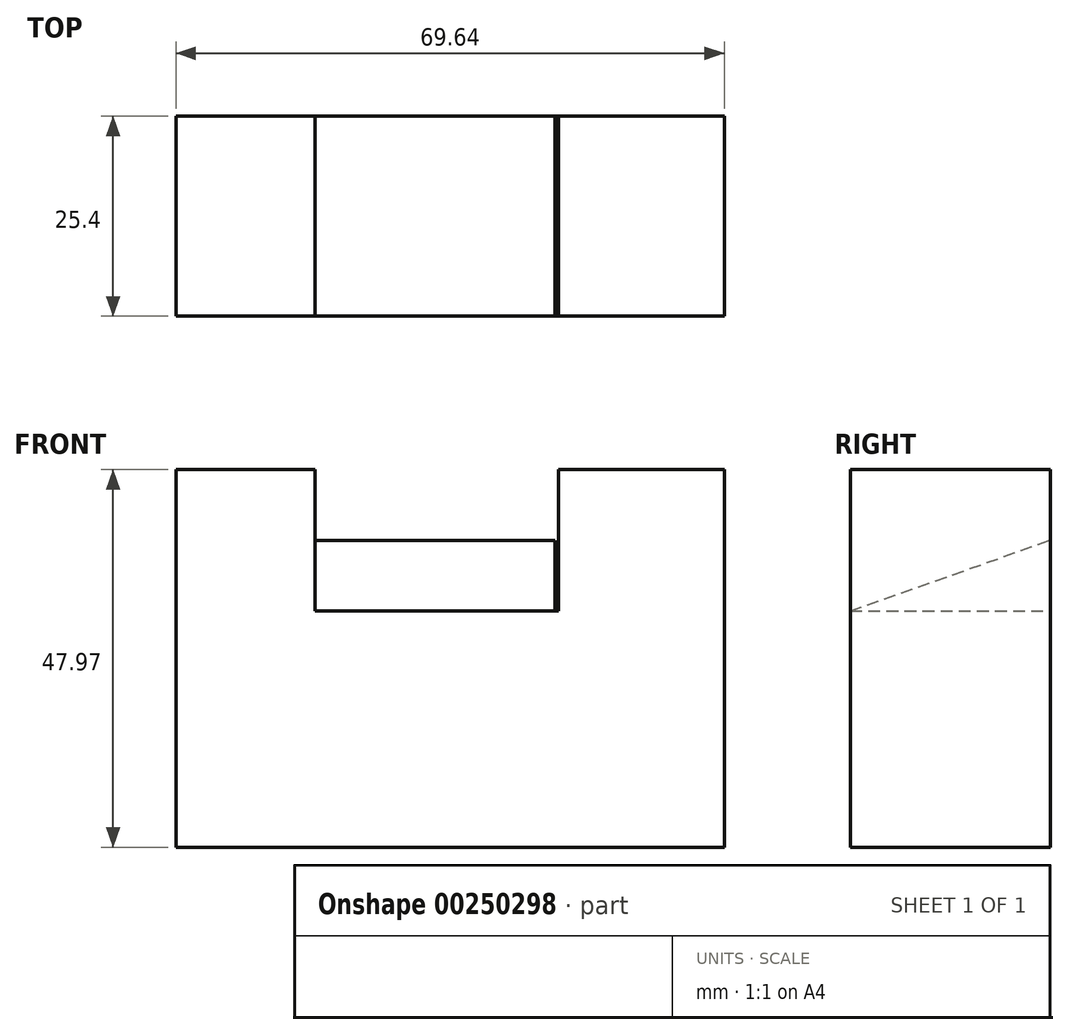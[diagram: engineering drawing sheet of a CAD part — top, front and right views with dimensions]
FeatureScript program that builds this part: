
annotation { "Feature Type Name" : "Feature", "Feature Type Description" : "" }
export const myFeature = defineFeature(function(context is Context, id is Id, definition is map)
    precondition{}
    {
        {
            var Q0;
            Q0=qCreatedBy(makeId("Front.planeOp"),FACE);
            var sketch = newSketch(context, id + "F0", { "sketchPlane" : qUnion([Q0])});
            skLineSegment(sketch, "E0", {"start": v(-48.6, 52.77) * mm, "end": v(-48.6, 3.87) * mm});
            skLineSegment(sketch, "E1", {"start": v(-48.6, 3.87) * mm, "end": v(21.05, 3.87) * mm});
            skLineSegment(sketch, "E2", {"start": v(21.05, 3.87) * mm, "end": v(21.05, 51.84) * mm});
            skLineSegment(sketch, "E3", {"start": v(21.05, 51.84) * mm, "end": v(0, 51.84) * mm});
            skLineSegment(sketch, "E4", {"start": v(0, 51.84) * mm, "end": v(0, 33.9) * mm});
            skLineSegment(sketch, "E5", {"start": v(0, 33.9) * mm, "end": v(-30.95, 33.9) * mm});
            skLineSegment(sketch, "E6", {"start": v(-30.95, 33.9) * mm, "end": v(-30.95, 51.84) * mm});
            skLineSegment(sketch, "E7", {"start": v(-30.95, 51.84) * mm, "end": v(-48.6, 51.84) * mm});
            skSolve(sketch);
        }
        {
            var Q0;
            {var subQ0=sQuery(id+"F0.wireOp",EDGE,"E1");Q0=makeQuery(id+"F0.imprint","IMPRINT",FACE,{"disambiguationData":[TD([[makeQuery(id+"F0.imprint","IMPRINT",EDGE,{"derivedFrom":subQ0}),1.0]])]});}
            extrude(context, id + "F1", {"entities" : qUnion([Q0]), "depth" : 25.4 * mm});
        }
        {
            var Q0;
            Q0=makeQuery(id+"F1.opExtrude","SWEPT_FACE",FACE,{"disambiguationData":[OSD([sQuery(id+"F0.wireOp",EDGE,"E6")])]});
            var sketch = newSketch(context, id + "F2", { "sketchPlane" : qUnion([Q0])});
            skLineSegment(sketch, "E8", {"start": v(-25.4, 33.9) * mm, "end": v(0, 42.87) * mm});
            skSolve(sketch);
        }
        {
            var Q0;
            {var subQ0=sQuery(id+"F2.wireOp",EDGE,"E8");Q0=makeQuery(id+"F2.imprint","IMPRINT",FACE,{"disambiguationData":[TD([[makeQuery(id+"F2.imprint","IMPRINT",EDGE,{"derivedFrom":subQ0}),-1.0]])]});}
            extrude(context, id + "F3", {"entities" : qUnion([Q0]), "operationType" : NewBodyOperationType.ADD, "depth" : 30.48 * mm});
        }
    });
